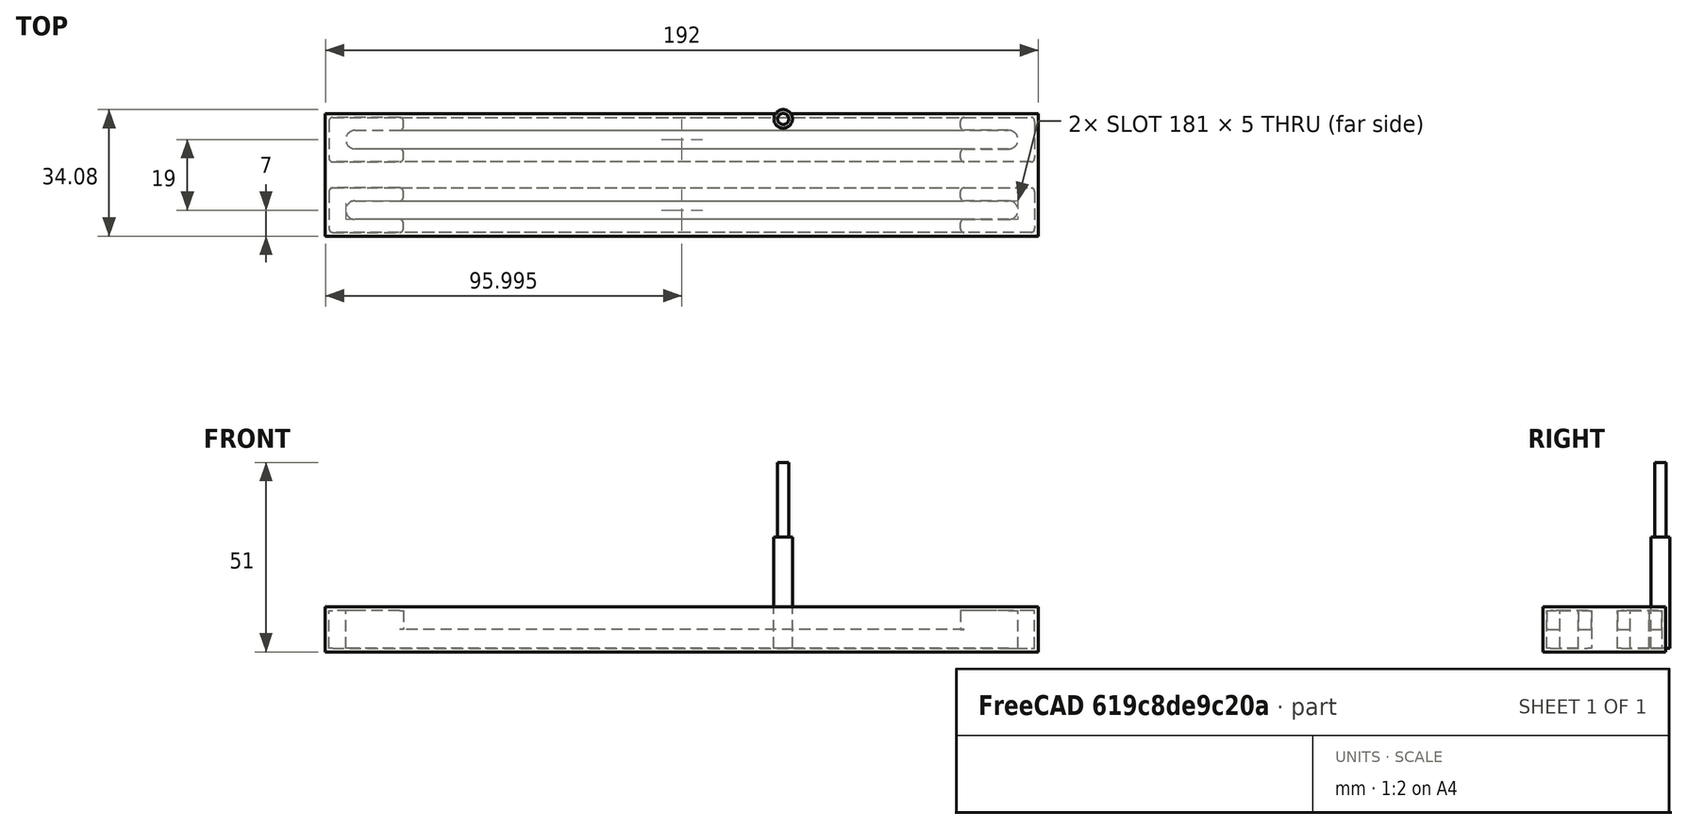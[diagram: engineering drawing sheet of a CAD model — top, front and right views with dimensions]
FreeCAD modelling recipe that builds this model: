
FCSTD DOCUMENT  (FreeCAD 1.0R39109 (Git))
Label: 25-06-03-usainageB_10mm
License: All rights reserved
LicenseURL: https://en.wikipedia.org/wiki/All_rights_reserved
objects: App::DocumentObjectGroup×3, Part::FeaturePython×3, Part::Feature×2, Path::FeaturePython×2, App::Part×1, App::FeaturePython×1
note: 5 computed .brp shape members not serialized (recipe doc carries the construction recipe); baked Part::Feature solids carry a one-line shape summary decoded from their .brp

FEATURE [Part::Feature] Part__Feature  label="rail_mobile_dessus_P.step"
  Placement = pos=(-27.2748,-5.57977,2.5) rot=(-1,0,0;1.5708rad)
  shape: bbox 190 x 12 x 10.1 mm, 29 faces (baked)
FEATURE [Part::Feature] Part__Feature001  label="rail_mobile_dessus_P.step001"
  Placement = pos=(-27.2748,-24.5798,2.5) rot=(-1,0,0;1.5708rad)
  shape: bbox 190 x 12 x 10.1 mm, 29 faces (baked)
FEATURE [App::Part] _5_06_03_usinageB_10mm  label="25-06-03-usinageB_10mm"
  Group = -> [Part__Feature,Part__Feature001]
  Origin = -> Origin
FEATURE [App::DocumentObjectGroup] Operations
FEATURE [App::FeaturePython] SetupSheet  # Path/CAM operation (typed FeaturePython)
  ClearanceHeightExpression = OpStockZMax+SetupSheet.ClearanceHeightOffset
  ClearanceHeightOffset = 5
  CoolantMode = 0
  CoolantModes = None | Flood | Mist
  FinalDepthExpression = OpFinalDepth
  HorizRapid = 0
  SafeHeightExpression = OpStockZMax+SetupSheet.SafeHeightOffset
  SafeHeightOffset = 3
  StartDepthExpression = OpStartDepth
  StepDownExpression = OpToolDiameter
  VertRapid = 0
FEATURE [Part::FeaturePython] Clone  label="Model-25-06-03-usinageB_10mm"  # Draft clone (typed FeaturePython)
  AttacherType = Attacher::AttachEngine3D
  Fuse = false
  Objects = -> [_5_06_03_usinageB_10mm]
  PathResource = Model
  Scale = (1,1,1)
FEATURE [App::DocumentObjectGroup] Model
  Group = -> [Clone]
FEATURE [Part::FeaturePython] ToolBit  label="Endmill"  # Path/CAM toolbit (typed FeaturePython)
  BitPropertyNames = Chipload | CuttingEdgeHeight | Diameter | Flutes | Length | Material | ShankDiameter | SpindleDirection
  BitShape = <userpath>\AppData\Local\Programs\FreeCAD 1.0\Mod\CAM\Tools\Shape\endmill.fcstd
  Chipload = 0
  CuttingEdgeHeight = 30
  Diameter = 5
  Flutes = 0
  Length = 50
  Material = 0
  ShankDiameter = 3
  ShapeName = endmill
  SpindleDirection = 0
FEATURE [Path::FeaturePython] TC__Default_Tool  label="TC: Default Tool"  # Path/CAM operation (typed FeaturePython)
  HorizFeed = 0
  HorizRapid = 0
  SpindleDir = 0
  SpindleSpeed = 0
  Tool = -> ToolBit
  ToolNumber = 1
  VertFeed = 0
  VertRapid = 0
  expr: HorizRapid = SetupSheet.HorizRapid
  expr: VertRapid = SetupSheet.VertRapid
FEATURE [App::DocumentObjectGroup] Tools
  Group = -> [TC__Default_Tool]
FEATURE [Part::FeaturePython] Stock  # WARN: FeaturePython — macro-defined, semantics opaque (R4)
  Base = -> Model
  ExtXneg = 1
  ExtXpos = 1
  ExtYneg = 1
  ExtYpos = 1
  ExtZneg = 1
  ExtZpos = 1
  Placement = pos=(-122.275,-30.5798,-2.2e-15) rot=(0,0,1;0rad)
  StockType = FromBase
FEATURE [Path::FeaturePython] Job  # Path/CAM operation (typed FeaturePython)
  CycleTime = 00:00:00
  Fixtures = G54
  GeometryTolerance = 0.01
  JobType = 0
  Model = -> Model
  Operations = -> Operations
  OrderOutputBy = 0
  PostProcessor = 25
  SetupSheet = -> SetupSheet
  SplitOutput = false
  Stock = -> Stock
  Tools = -> Tools
